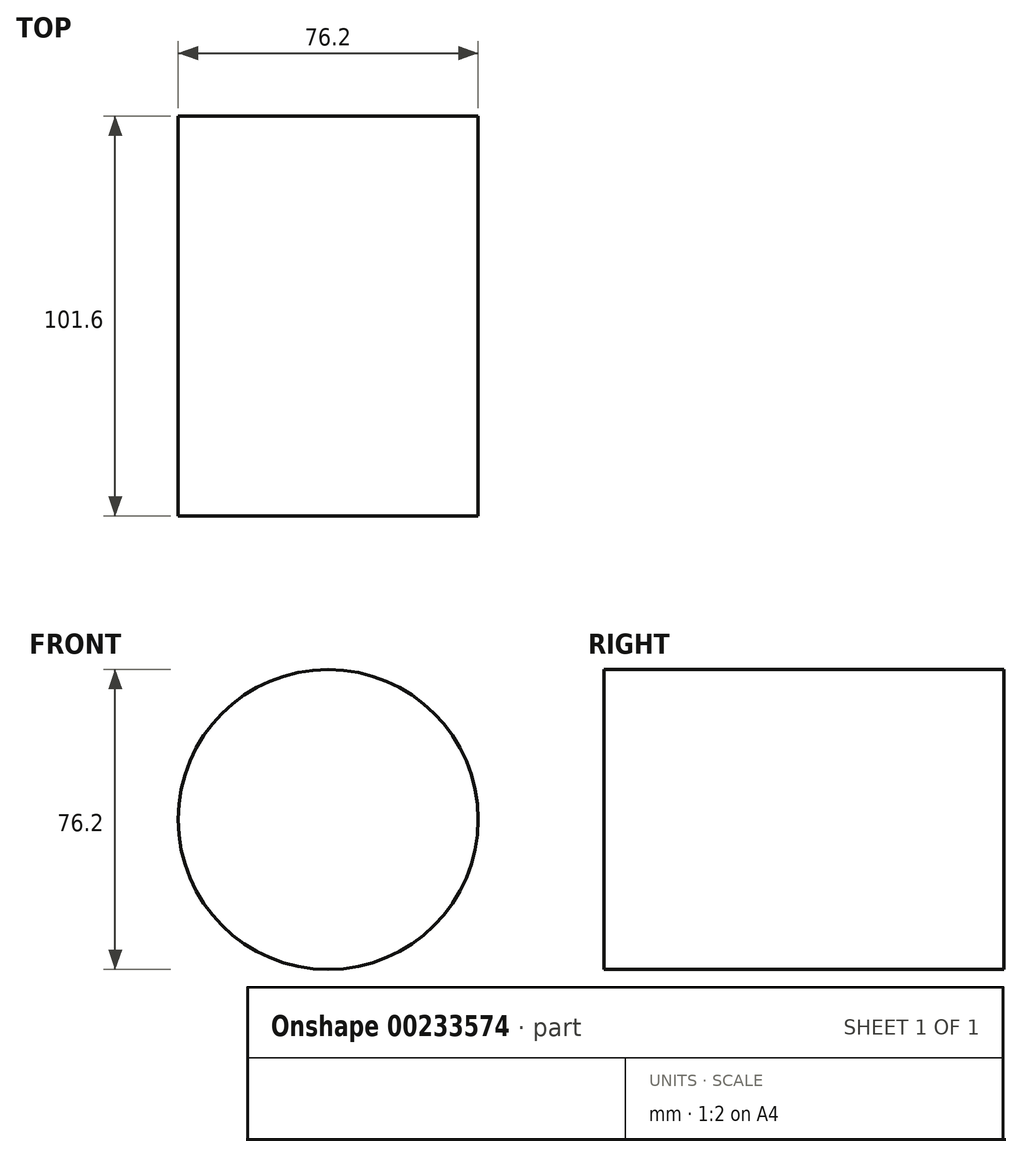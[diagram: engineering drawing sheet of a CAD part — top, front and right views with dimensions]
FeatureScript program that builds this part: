
annotation { "Feature Type Name" : "Feature", "Feature Type Description" : "" }
export const myFeature = defineFeature(function(context is Context, id is Id, definition is map)
    precondition{}
    {
        {
            var Q0;
            Q0=qCreatedBy(makeId("Front.planeOp"),FACE);
            var sketch = newSketch(context, id + "F0", { "sketchPlane" : qUnion([Q0])});
            skCircle(sketch, "E0", {"center": v(0, 0) * mm, "radius": 38.1 * mm});
            skSolve(sketch);
        }
        {
            var Q0;
            Q0=makeQuery(id+"F0.imprint","IMPRINT",FACE,{"disambiguationData":[TD([[makeQuery(id+"F0.imprint","IMPRINT",EDGE,{"derivedFrom":sQuery(id+"F0.wireOp",EDGE,"E0")}),1.0]])]});
            extrude(context, id + "F1", {"entities" : qUnion([Q0]), "depth" : 101.6 * mm});
        }
    });
